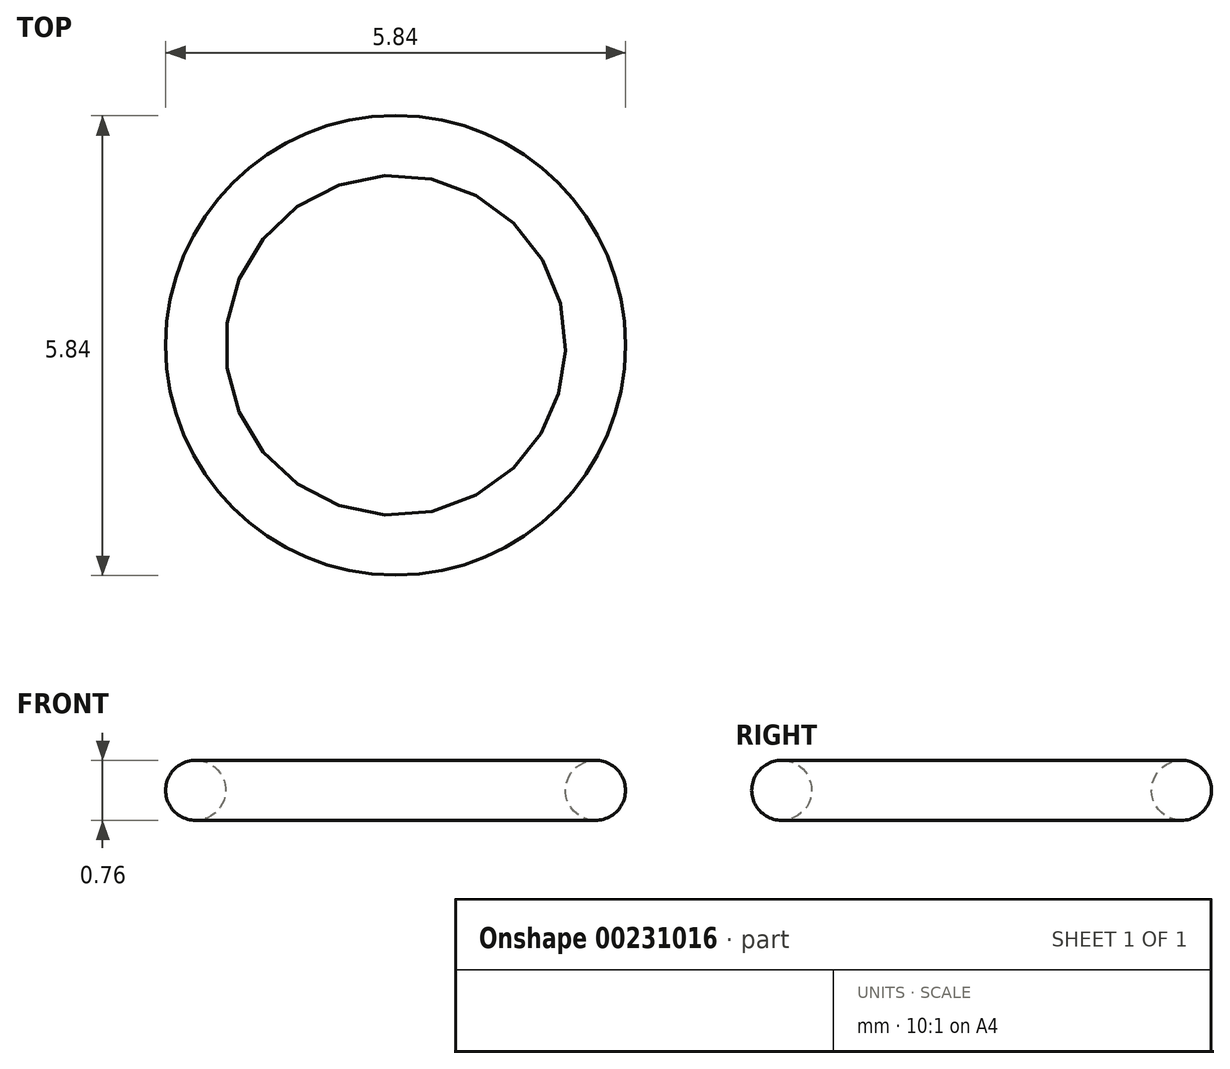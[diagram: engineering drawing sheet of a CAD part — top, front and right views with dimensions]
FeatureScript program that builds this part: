
annotation { "Feature Type Name" : "Feature", "Feature Type Description" : "" }
export const myFeature = defineFeature(function(context is Context, id is Id, definition is map)
    precondition{}
    {
        {
            var Q0;
            Q0=qCreatedBy(makeId("Front.planeOp"),FACE);
            var sketch = newSketch(context, id + "F0", { "sketchPlane" : qUnion([Q0])});
            skCircle(sketch, "E0", {"center": v(0, 0) * mm, "radius": 0.38 * mm});
            skSolve(sketch);
        }
        {
            var Q0;
            Q0=qCreatedBy(makeId("Top.planeOp"),FACE);
            var sketch = newSketch(context, id + "F1", { "sketchPlane" : qUnion([Q0])});
            skCircle(sketch, "E1", {"center": v(2.54, -0.08) * mm, "radius": 2.54 * mm});
            skPoint(sketch, "E1.first.point", {"position": v(0, 0) * mm});
            skPoint(sketch, "E1.second.point", {"position": v(5.06, -0.35) * mm});
            skPoint(sketch, "E1.third.point", {"position": v(4.6, 1.42) * mm});
            skSolve(sketch);
        }
        {
            var Q0;
            Q0=makeQuery(id+"F0.imprint","IMPRINT",FACE,{"disambiguationData":[TD([[makeQuery(id+"F0.imprint","IMPRINT",EDGE,{"derivedFrom":sQuery(id+"F0.wireOp",EDGE,"E0")}),1.0]])]});
            var Q1;
            Q1=sQuery(id+"F1.wireOp",EDGE,"E1");
            sweep(context, id + "F2", {"profiles" : qUnion([Q0]), "path" : qUnion([Q1])});
        }
    });
